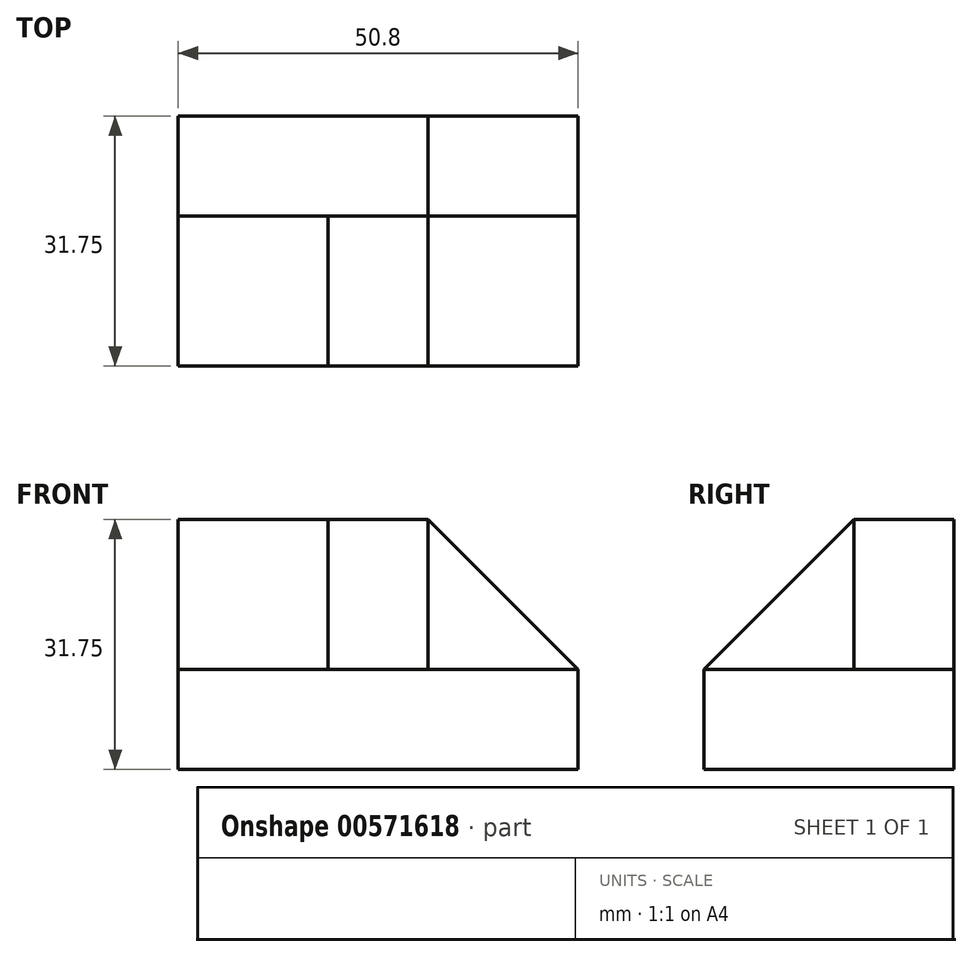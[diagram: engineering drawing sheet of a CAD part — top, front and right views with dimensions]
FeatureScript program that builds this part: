
annotation { "Feature Type Name" : "Feature", "Feature Type Description" : "" }
export const myFeature = defineFeature(function(context is Context, id is Id, definition is map)
    precondition{}
    {
        {
            var Q0;
            Q0=qCreatedBy(makeId("Front.planeOp"),FACE);
            var sketch = newSketch(context, id + "F0", { "sketchPlane" : qUnion([Q0])});
            skLineSegment(sketch, "E0", {"start": v(-50.8, 41.22) * mm, "end": v(-50.8, 9.47) * mm});
            skLineSegment(sketch, "E1", {"start": v(-50.8, 9.47) * mm, "end": v(0, 9.47) * mm});
            skLineSegment(sketch, "E2", {"start": v(0, 9.47) * mm, "end": v(0, 41.22) * mm});
            skLineSegment(sketch, "E3", {"start": v(0, 41.22) * mm, "end": v(-50.8, 41.22) * mm});
            skSolve(sketch);
        }
        {
            var Q0;
            Q0 = qSketchRegion(id + "F0", true);
            extrude(context, id + "F1", {"entities" : qUnion([Q0]), "depth" : 31.75 * mm, "offsetDistance" : 25.4 * mm});
        }
        {
            var Q0;
            Q0=makeQuery(id+"F1.opExtrude","SWEPT_FACE",FACE,{"disambiguationData":[OSD([sQuery(id+"F0.wireOp",EDGE,"E0")])]});
            var sketch = newSketch(context, id + "F2", { "sketchPlane" : qUnion([Q0])});
            skLineSegment(sketch, "E4", {"start": v(12.7, 41.22) * mm, "end": v(12.7, 22.17) * mm});
            skLineSegment(sketch, "E5", {"start": v(12.7, 22.17) * mm, "end": v(31.75, 22.17) * mm});
            skLineSegment(sketch, "E6", {"start": v(31.75, 22.17) * mm, "end": v(31.75, 41.22) * mm});
            skLineSegment(sketch, "E7", {"start": v(31.75, 41.22) * mm, "end": v(12.7, 41.22) * mm});
            skSolve(sketch);
        }
        {
            var Q0;
            Q0 = qSketchRegion(id + "F2", true);
            extrude(context, id + "F3", {"entities" : qUnion([Q0]), "operationType" : NewBodyOperationType.REMOVE, "oppositeDirection" : true, "depth" : 19.05 * mm, "offsetDistance" : 25.4 * mm});
        }
        {
            var Q0;
            Q0=makeQuery(id+"F3.boolean.opBoolean","COPY",FACE,{"derivedFrom":makeQuery(id+"F3.opExtrude","CAP_FACE",FACE,{"disambiguationData":[OSD([sQuery(id+"F2.wireOp",EDGE,"E4"),sQuery(id+"F2.wireOp",EDGE,"E5"),sQuery(id+"F2.wireOp",EDGE,"E6"),sQuery(id+"F2.wireOp",EDGE,"E7")])],"isStart":false})});
            var sketch = newSketch(context, id + "F4", { "sketchPlane" : qUnion([Q0])});
            skLineSegment(sketch, "E8", {"start": v(12.7, 41.22) * mm, "end": v(31.75, 22.17) * mm});
            skLineSegment(sketch, "E9", {"start": v(31.75, 22.17) * mm, "end": v(31.75, 41.22) * mm});
            skLineSegment(sketch, "E10", {"start": v(31.75, 41.22) * mm, "end": v(12.7, 41.22) * mm});
            skSolve(sketch);
        }
        {
            var Q0;
            Q0 = qSketchRegion(id + "F4", true);
            extrude(context, id + "F5", {"entities" : qUnion([Q0]), "operationType" : NewBodyOperationType.REMOVE, "oppositeDirection" : true, "depth" : 12.7 * mm, "offsetDistance" : 25.4 * mm});
        }
        {
            var Q0;
            Q0=makeQuery(id+"F1.opExtrude","SWEPT_FACE",FACE,{"disambiguationData":[OSD([sQuery(id+"F0.wireOp",EDGE,"E2")])]});
            var sketch = newSketch(context, id + "F6", { "sketchPlane" : qUnion([Q0])});
            skLineSegment(sketch, "E11", {"start": v(-12.7, 41.22) * mm, "end": v(-12.7, 22.17) * mm});
            skLineSegment(sketch, "E12", {"start": v(-12.7, 22.17) * mm, "end": v(-31.75, 22.17) * mm});
            skLineSegment(sketch, "E13", {"start": v(-31.75, 22.17) * mm, "end": v(-31.75, 41.22) * mm});
            skLineSegment(sketch, "E14", {"start": v(-31.75, 41.22) * mm, "end": v(-12.7, 41.22) * mm});
            skSolve(sketch);
        }
        {
            var Q0;
            Q0 = qSketchRegion(id + "F6", true);
            extrude(context, id + "F7", {"entities" : qUnion([Q0]), "operationType" : NewBodyOperationType.REMOVE, "oppositeDirection" : true, "depth" : 19.05 * mm, "offsetDistance" : 25.4 * mm});
        }
        {
            var Q0;
            Q0=makeQuery(id+"F1.opExtrude","CAP_FACE",FACE,{"disambiguationData":[OSD([sQuery(id+"F0.wireOp",EDGE,"E0"),sQuery(id+"F0.wireOp",EDGE,"E1"),sQuery(id+"F0.wireOp",EDGE,"E2"),sQuery(id+"F0.wireOp",EDGE,"E3")])],"isStart":true});
            var sketch = newSketch(context, id + "F8", { "sketchPlane" : qUnion([Q0])});
            skLineSegment(sketch, "E15", {"start": v(19.05, 41.22) * mm, "end": v(0, 41.22) * mm});
            skLineSegment(sketch, "E16", {"start": v(0, 41.22) * mm, "end": v(0, 22.17) * mm});
            skLineSegment(sketch, "E17", {"start": v(0, 22.17) * mm, "end": v(19.05, 41.22) * mm});
            skSolve(sketch);
        }
        {
            var Q0;
            Q0 = qSketchRegion(id + "F8", true);
            extrude(context, id + "F9", {"entities" : qUnion([Q0]), "operationType" : NewBodyOperationType.REMOVE, "oppositeDirection" : true, "depth" : 12.7 * mm, "offsetDistance" : 25.4 * mm});
        }
    });
